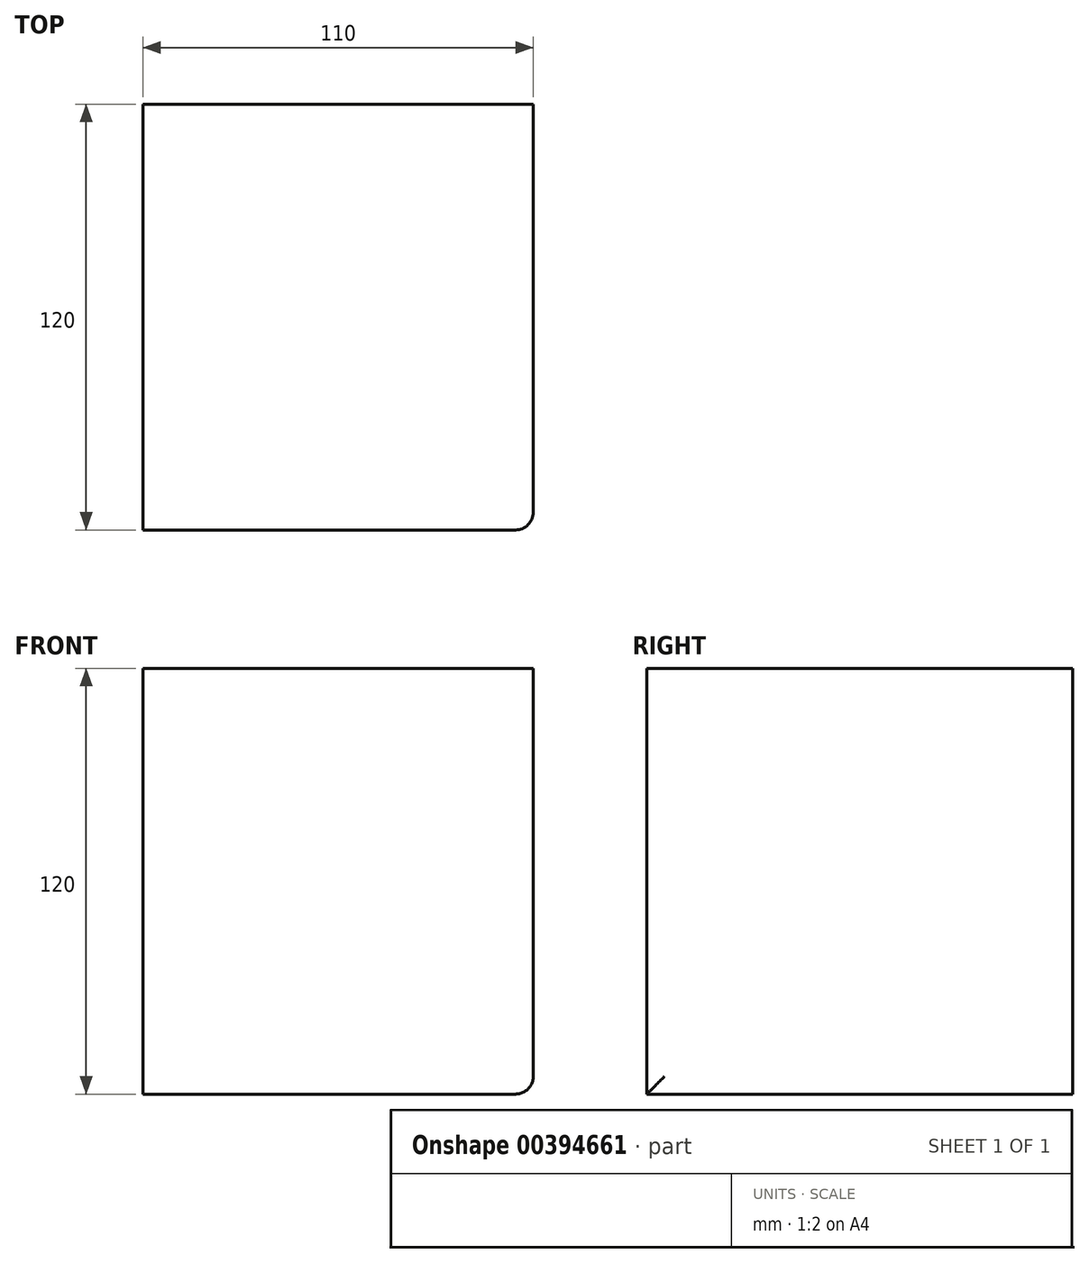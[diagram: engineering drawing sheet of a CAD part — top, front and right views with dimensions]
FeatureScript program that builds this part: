
annotation { "Feature Type Name" : "Feature", "Feature Type Description" : "" }
export const myFeature = defineFeature(function(context is Context, id is Id, definition is map)
    precondition{}
    {
        {
            var Q0;
            Q0=qCreatedBy(makeId("Right.planeOp"),FACE);
            var sketch = newSketch(context, id + "F0", { "sketchPlane" : qUnion([Q0])});
            skLineSegment(sketch, "E0.bottom", {"start": v(-60, 60) * mm, "end": v(60, 60) * mm});
            skLineSegment(sketch, "E0.top", {"start": v(-60, -60) * mm, "end": v(60, -60) * mm});
            skLineSegment(sketch, "E0.left", {"start": v(-60, 60) * mm, "end": v(-60, -60) * mm});
            skLineSegment(sketch, "E0.right", {"start": v(60, 60) * mm, "end": v(60, -60) * mm});
            skSolve(sketch);
        }
        {
            var Q0;
            Q0=makeQuery(id+"F0.imprint","IMPRINT",FACE,{"disambiguationData":[TD([[makeQuery(id+"F0.imprint","IMPRINT",EDGE,{"derivedFrom":sQuery(id+"F0.wireOp",EDGE,"E0.bottom")}),-1.0]])]});
            extrude(context, id + "F1", {"entities" : qUnion([Q0]), "depth" : 110 * mm});
        }
        {
            var Q0;
            Q0=makeQuery(id+"F1.opExtrude","CAP_EDGE",EDGE,{"disambiguationData":[OSD([sQuery(id+"F0.wireOp",EDGE,"E0.left")])],"isStart":false});
            var Q1;
            Q1=makeQuery(id+"F1.opExtrude","CAP_EDGE",EDGE,{"disambiguationData":[OSD([sQuery(id+"F0.wireOp",EDGE,"E0.top")])],"isStart":false});
            fillet(context, id + "F2", {"entities" : qUnion([Q0, Q1]), "radius" : 5 * mm, "tangentPropagation" : true, "allowEdgeOverflow" : false});
        }
    });
